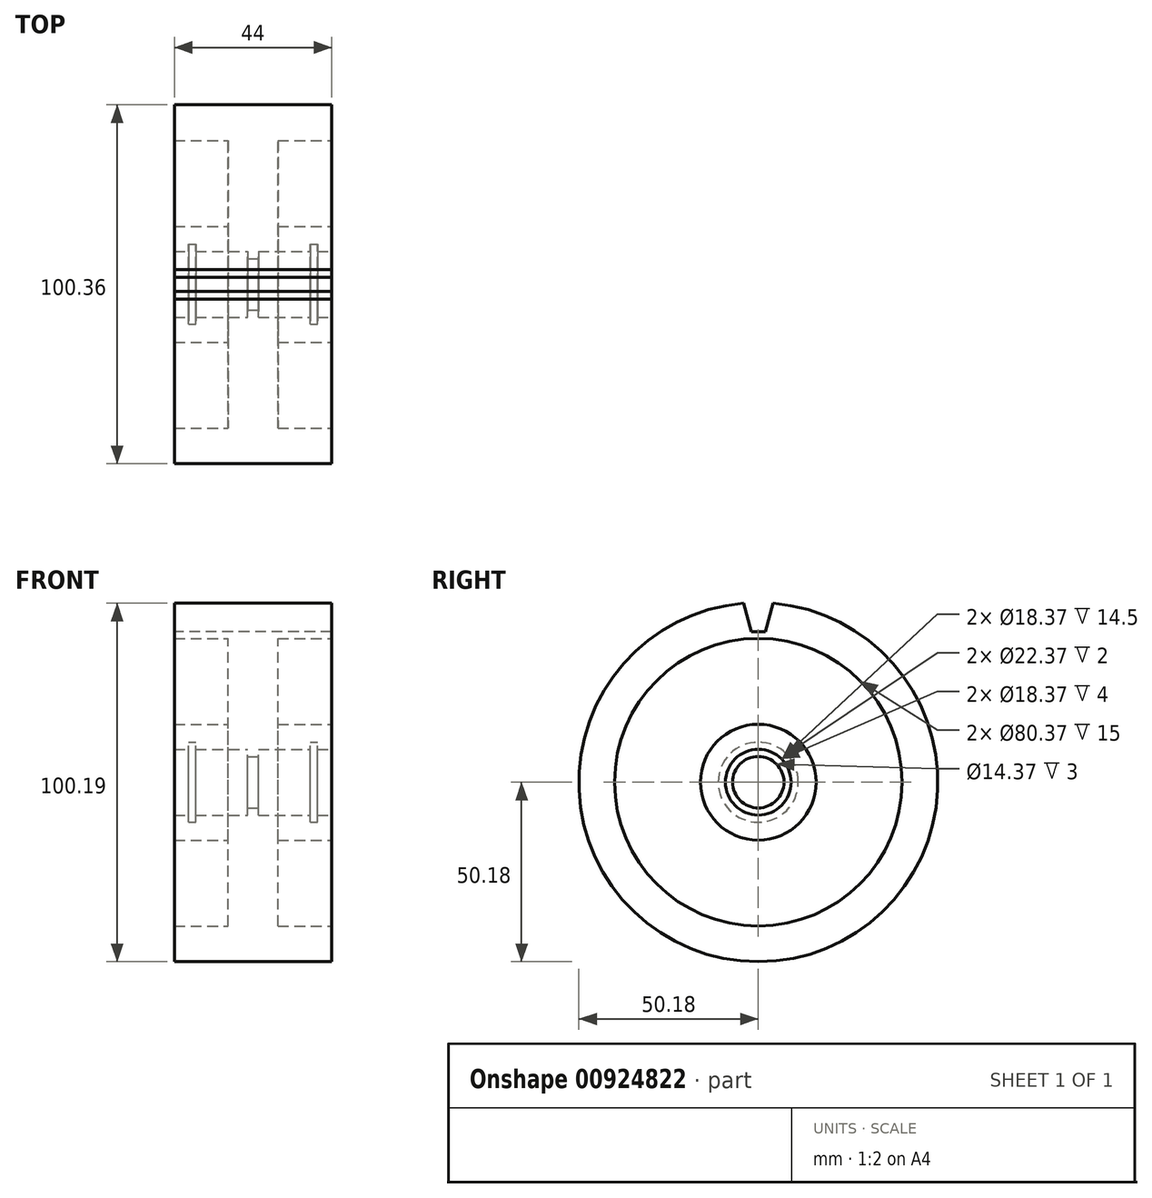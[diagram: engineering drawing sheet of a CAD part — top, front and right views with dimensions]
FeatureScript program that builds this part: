
annotation { "Feature Type Name" : "Feature", "Feature Type Description" : "" }
export const myFeature = defineFeature(function(context is Context, id is Id, definition is map)
    precondition{}
    {
        {
            var Q0;
            Q0=qCreatedBy(makeId("Front.planeOp"),FACE);
            var sketch = newSketch(context, id + "F0", { "sketchPlane" : qUnion([Q0])});
            skLineSegment(sketch, "E0", {"start": v(0, 50.18) * mm, "end": v(-22, 50.18) * mm});
            skLineSegment(sketch, "E1", {"start": v(0, 50.18) * mm, "end": v(22, 50.18) * mm});
            skLineSegment(sketch, "E2", {"start": v(22, 50.18) * mm, "end": v(22, 40.18) * mm});
            skLineSegment(sketch, "E3", {"start": v(22, 40.18) * mm, "end": v(7, 40.18) * mm});
            skLineSegment(sketch, "E4", {"start": v(7, 40.18) * mm, "end": v(7, 16.18) * mm});
            skLineSegment(sketch, "E5", {"start": v(7, 16.18) * mm, "end": v(22, 16.18) * mm});
            skLineSegment(sketch, "E6", {"start": v(22, 16.18) * mm, "end": v(22, 9.18) * mm});
            skLineSegment(sketch, "E7", {"start": v(22, 9.18) * mm, "end": v(18, 9.18) * mm});
            skLineSegment(sketch, "E8", {"start": v(18, 9.18) * mm, "end": v(18, 11.18) * mm});
            skLineSegment(sketch, "E9", {"start": v(18, 11.18) * mm, "end": v(16, 11.18) * mm});
            skLineSegment(sketch, "E10", {"start": v(16, 11.18) * mm, "end": v(16, 9.18) * mm});
            skLineSegment(sketch, "E11", {"start": v(16, 9.18) * mm, "end": v(1.5, 9.18) * mm});
            skLineSegment(sketch, "E12", {"start": v(1.5, 9.18) * mm, "end": v(1.5, 7.18) * mm});
            skLineSegment(sketch, "E13", {"start": v(1.5, 7.18) * mm, "end": v(0, 7.18) * mm});
            skLineSegment(sketch, "E14.MirrorCS", {"start": v(-18, 11.18) * mm, "end": v(-16, 11.18) * mm});
            skLineSegment(sketch, "E15.MirrorCS", {"start": v(-18, 9.18) * mm, "end": v(-18, 11.18) * mm});
            skLineSegment(sketch, "E16.MirrorCS", {"start": v(-22, 9.18) * mm, "end": v(-18, 9.18) * mm});
            skLineSegment(sketch, "E17.MirrorCS", {"start": v(-16, 11.18) * mm, "end": v(-16, 9.18) * mm});
            skLineSegment(sketch, "E18.MirrorCS", {"start": v(-16, 9.18) * mm, "end": v(-1.5, 9.18) * mm});
            skLineSegment(sketch, "E19.MirrorCS", {"start": v(-7, 40.18) * mm, "end": v(-7, 16.18) * mm});
            skLineSegment(sketch, "E20.MirrorCS", {"start": v(-7, 16.18) * mm, "end": v(-22, 16.18) * mm});
            skLineSegment(sketch, "E21.MirrorCS", {"start": v(-22, 16.18) * mm, "end": v(-22, 9.18) * mm});
            skLineSegment(sketch, "E22.MirrorCS", {"start": v(-22, 50.18) * mm, "end": v(-22, 40.18) * mm});
            skLineSegment(sketch, "E23.MirrorCS", {"start": v(-22, 40.18) * mm, "end": v(-7, 40.18) * mm});
            skLineSegment(sketch, "E24", {"start": v(-1.5, 9.18) * mm, "end": v(-1.5, 7.18) * mm});
            skLineSegment(sketch, "E25", {"start": v(-1.5, 7.18) * mm, "end": v(0, 7.18) * mm});
            skLineSegment(sketch, "E26", {"start": v(0, 7.18) * mm, "end": v(0, 0) * mm, "construction": true});
            skLineSegment(sketch, "E27", {"start": v(0, 0) * mm, "end": v(-14.08, 0) * mm, "construction": true});
            skLineSegment(sketch, "E28", {"start": v(0, 7.18) * mm, "end": v(0, 0) * mm});
            skSolve(sketch);
        }
        {
            var Q0;
            Q0=makeQuery(id+"F0.imprint","IMPRINT",FACE,{"disambiguationData":[TD([[makeQuery(id+"F0.imprint","IMPRINT",EDGE,{"derivedFrom":sQuery(id+"F0.wireOp",EDGE,"E1")}),-1.0]])]});
            var Q1;
            Q1=sQuery(id+"F0.wireOp",EDGE,"E27");
            revolve(context, id + "F1", {"surfaceOperationType" : NewSurfaceOperationType.NEW, "entities" : qUnion([Q0]), "axis" : qUnion([Q1]), "revolveType" : RevolveType.FULL});
        }
        {
            var Q0;
            Q0=qCreatedBy(makeId("Right.planeOp"),FACE);
            var sketch = newSketch(context, id + "F2", { "sketchPlane" : qUnion([Q0])});
            skLineSegment(sketch, "E29", {"start": v(0, 42.13) * mm, "end": v(2, 42.13) * mm});
            skLineSegment(sketch, "E30", {"start": v(0, 42.13) * mm, "end": v(-2, 42.13) * mm});
            skLineSegment(sketch, "E31", {"start": v(0, 53.13) * mm, "end": v(-5, 53.13) * mm});
            skLineSegment(sketch, "E32", {"start": v(0, 53.13) * mm, "end": v(5, 53.13) * mm});
            skLineSegment(sketch, "E33", {"start": v(5, 53.13) * mm, "end": v(2, 42.13) * mm});
            skLineSegment(sketch, "E34", {"start": v(-5, 53.13) * mm, "end": v(-2, 42.13) * mm});
            skSolve(sketch);
        }
        {
            var Q0;
            Q0 = qSketchRegion(id + "F2", true);
            extrude(context, id + "F3", {"entities" : qUnion([Q0]), "operationType" : NewBodyOperationType.REMOVE, "endBound" : BoundingType.SYMMETRIC, "depth" : 97.2 * mm, "offsetDistance" : 25 * mm});
        }
    });
